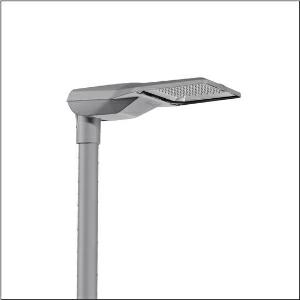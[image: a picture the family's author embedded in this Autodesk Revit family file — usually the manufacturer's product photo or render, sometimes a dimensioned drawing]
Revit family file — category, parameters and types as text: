
# Revit family: streetlight_sl_21_midi___st0_8a_5xe7c33a08mb_9d26
name_source: partatom
category: Lighting Fixtures
units: mm (PartAtom-declared; Revit-internal decimal feet)

## family parameters
Cut with Voids When Loaded = No
Host = Face
Light Source = No
Part Type = Normal
Room Calculation Point = No
Round Connector Dimension = Use Diameter
Shared = No

## types (1)
- --- (1 x LED, 18270 lm, 136 W, 3000K)
    Apparent Load = 136 VA
    CIE Flux Codes = 38 75 97 100 100
    Color Rendering = 70
    Color Temperature = 3000K
    Default Elevation = 1800 mm
    Description = Streetlight SL 21 midi, mast luminaire, primary light control with lens, of PMMA, primary optical cover: cover, of toughened safety glass, transparent, light distribution: ST0.8a, light emission: direct distribution, primary light characteristic: asymmetric, installation type: post-top, side-entry, LED, 3G 1.5mm², High Power LED, rated luminous flux: 18.270lm, luminous efficacy: 134lm/W, light colour: 730, colour temperature: 3000K, control: overheat protection, constant luminous flux control, time-dependent luminous flux control, flexible luminous flux parameterisation, mains connection: 220..240V, AC, 50/60Hz, connection cable pre-assembled, cable length: 12,5m, wiring characteristics: H07RN-F, start of lifetime: 136W, end of service life: 142W, reduction: 61W, luminaire housing, of diecast aluminium, powder-coated, Siteco® metallic grey (DB 702S), corrosivity category C5 mid according to DIN EN ISO 12944, please order mast flange separately, inclination adjustable: 0°, 5°, 10°, 15°, sealing non-destructively replaceable, multi-level sealing system, length: 644mm, width: 335mm, height: 110mm, mast flange for spigot size: 42mm (side-entry): 5XC10008XM4, 60/48mm (side-entry/post-top): 5XC10108XM2, 76/60mm (side-entry/post-top): 5XC10108XM1, protection rating (complete): IP66, insulation class (complete): insulation class II (safety insulation), certification: CE, ENEC, ENEC+, VDE, impact resistance: IK09, permissible operating ambient temperature for outdoor applications: -40..+50°C, standard-compliant lighting for roads and squares, packaging unit: 1 piece

Light Distribution: ST0.8a
    Height = 111 mm
    Lamp = 1 x LED
    Lamp Light Flux = 18270 lm
    Lamp Power = 136 W
    Lamp count = 1
    Length = 644 mm
    Luminous efficacy = 134 lm/W
    Manufacturer = Siteco
    ModVariant = No
    Model = 5XE7C33A08MB
    Number of Poles = 1
    OnlyDefault = Yes
    Power Factor = 1
    Product Name = Streetlight SL 21 midi | ST0.8a
    Product group = mast luminaire | pylon top
    ProductGroupID = 6100
    Protection Class = Protection class II
    Protection Degree = IP 66
    RLX_Detail_Level = 1
    RLX_Emergency_Light_Flux = 0 lm
    RLX_Emergency_Type = 0
    RLX_Emergency_Type_DB = No
    RlxData = <blob elided: 90973 chars, md5=d2375a73>
    Socket = socket
    Standby Power = 0 W
    System Light Flux = 18270 lm
    System Power = 136 W
    Type Comments = factory setting: luminous flux: 100 % | Output Level: 100 % | 695 mA
    Type Image = l_1004298.jpg
    URL = http://relux.com
    VarID = @adj_137395
    Voltage = 0 V
    Weight = 0.00 kg
    Width = 336 mm

## geometry (parser evidence)
native form markers: Blend x4, Sweep x13
no freeform markers — native parametric forms only
